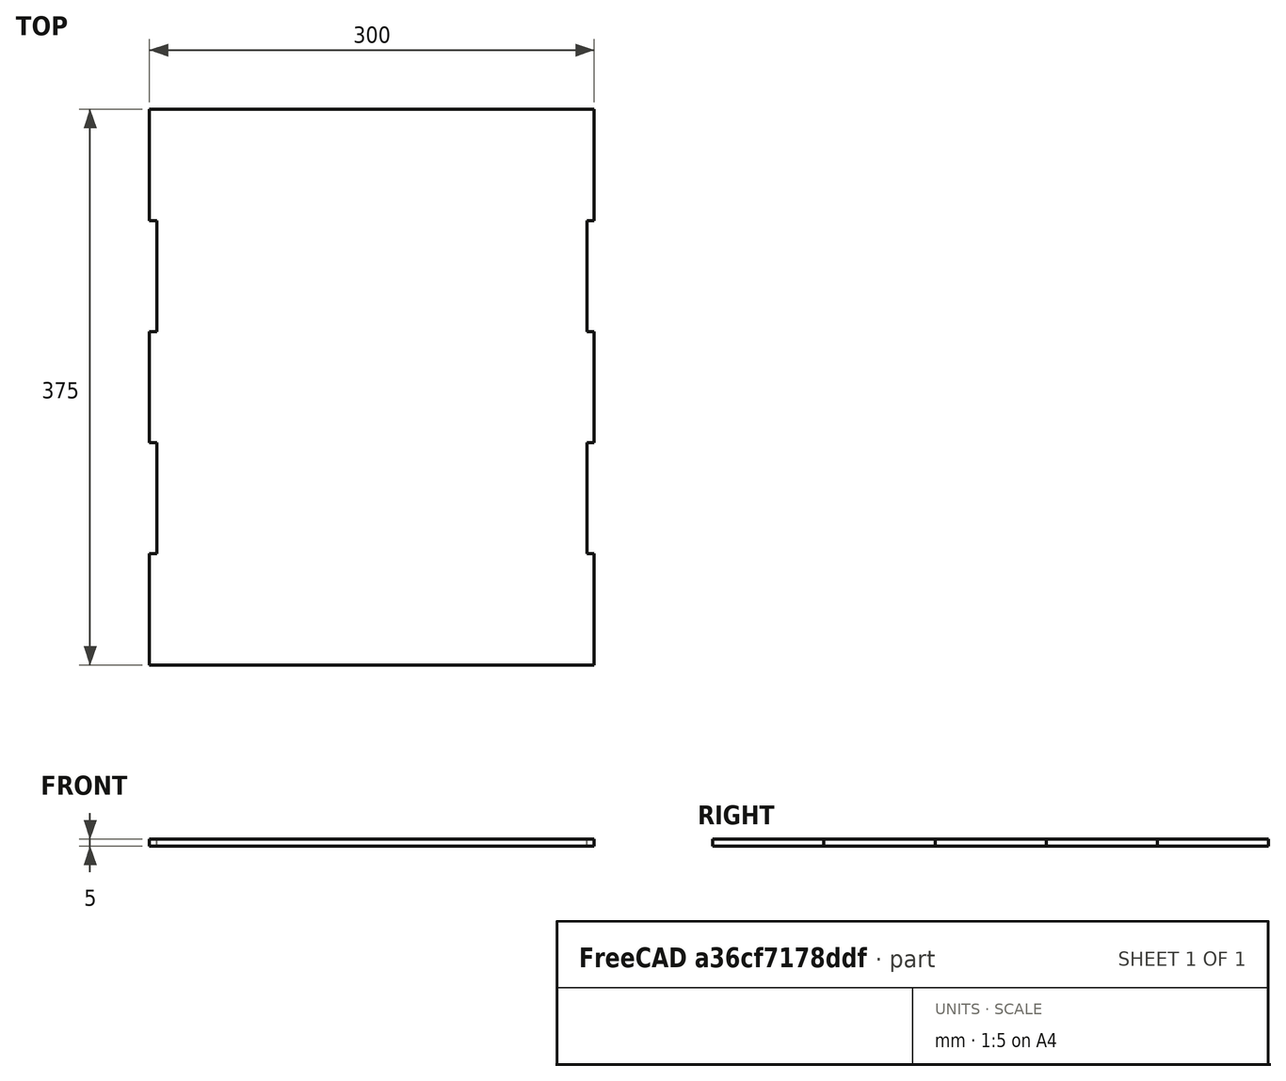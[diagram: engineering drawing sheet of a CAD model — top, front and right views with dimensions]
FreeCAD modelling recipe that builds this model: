
FCSTD DOCUMENT  (FreeCAD 0.18R4 (GitTag))
Label: Chassis
License: All rights reserved
LicenseURL: http://en.wikipedia.org/wiki/All_rights_reserved
objects: Sketcher::SketchObject×2, PartDesign::Pad×1, PartDesign::Body×1
note: 5 computed .brp shape members not serialized (recipe doc carries the construction recipe); baked Part::Feature solids carry a one-line shape summary decoded from their .brp

FEATURE [Sketcher::SketchObject] Sketch
  MapMode = 2
  Support = -> [Sketch]
  sketch-geometry (20):
    g0: LineSegment StartX=-83.8365 StartY=179.356 StartZ=0 EndX=-83.8365 EndY=104.356 EndZ=0
    g1: LineSegment StartX=-83.8365 StartY=104.356 StartZ=0 EndX=-78.8365 EndY=104.356 EndZ=0
    g2: LineSegment StartX=-78.8365 StartY=104.356 StartZ=0 EndX=-78.8365 EndY=29.3556 EndZ=0
    g3: LineSegment StartX=-78.8365 StartY=29.3556 StartZ=0 EndX=-83.8365 EndY=29.3556 EndZ=0
    g4: LineSegment StartX=-83.8365 StartY=29.3556 StartZ=0 EndX=-83.8365 EndY=-45.6444 EndZ=0
    g5: LineSegment StartX=-83.8365 StartY=-45.6444 StartZ=0 EndX=-78.8365 EndY=-45.6444 EndZ=0
    g6: LineSegment StartX=-78.8365 StartY=-45.6444 StartZ=0 EndX=-78.8365 EndY=-120.644 EndZ=0
    g7: LineSegment StartX=-78.8365 StartY=-120.644 StartZ=0 EndX=-83.8365 EndY=-120.644 EndZ=0
    g8: LineSegment StartX=-83.8365 StartY=-120.644 StartZ=0 EndX=-83.8365 EndY=-195.644 EndZ=0
    g9: LineSegment StartX=-83.8365 StartY=-195.644 StartZ=0 EndX=216.163 EndY=-195.644 EndZ=0
    g10: LineSegment StartX=216.163 StartY=-195.644 StartZ=0 EndX=216.163 EndY=-120.644 EndZ=0
    g11: LineSegment StartX=216.163 StartY=-120.644 StartZ=0 EndX=211.163 EndY=-120.644 EndZ=0
    g12: LineSegment StartX=211.163 StartY=-120.644 StartZ=0 EndX=211.163 EndY=-45.6444 EndZ=0
    g13: LineSegment StartX=211.163 StartY=-45.6444 StartZ=0 EndX=216.163 EndY=-45.6444 EndZ=0
    g14: LineSegment StartX=216.163 StartY=-45.6444 StartZ=0 EndX=216.163 EndY=29.3556 EndZ=0
    g15: LineSegment StartX=216.163 StartY=29.3556 StartZ=0 EndX=211.163 EndY=29.3556 EndZ=0
    g16: LineSegment StartX=211.163 StartY=29.3556 StartZ=0 EndX=211.163 EndY=104.356 EndZ=0
    g17: LineSegment StartX=211.163 StartY=104.356 StartZ=0 EndX=216.163 EndY=104.356 EndZ=0
    g18: LineSegment StartX=216.163 StartY=104.356 StartZ=0 EndX=216.163 EndY=179.356 EndZ=0
    g19: LineSegment StartX=216.163 StartY=179.356 StartZ=0 EndX=-83.8365 EndY=179.356 EndZ=0
  constraints (58):
    c: Coincident(g0,g1)
    c: Coincident(g1,g2)
    c: Coincident(g2,g3)
    c: Coincident(g3,g4)
    c: Coincident(g4,g5)
    c: Coincident(g5,g6)
    c: Coincident(g6,g7)
    c: Coincident(g7,g8)
    c: Coincident(g8,g9)
    c: Coincident(g9,g10)
    c: Coincident(g10,g11)
    c: Coincident(g11,g12)
    c: Coincident(g12,g13)
    c: Coincident(g13,g14)
    c: Coincident(g14,g15)
    c: Coincident(g15,g16)
    c: Coincident(g16,g17)
    c: Coincident(g17,g18)
    c: Coincident(g18,g19)
    c: Coincident(g19,g0)
    c: DistanceX(g17,g17) = 5
    c: DistanceX(g15,g15) = 5
    c: DistanceX(g13,g13) = 5
    c: DistanceX(g11,g11) = 5
    c: DistanceX(g7,g7) = 5
    c: DistanceX(g5,g5) = 5
    c: DistanceX(g3,g3) = 5
    c: DistanceX(g1,g1) = 5
    c: Angle(g18,g17) = 1.5708
    c: Angle(g15,g16) = 1.5708
    c: Angle(g19,g16) = 1.5708
    c: Angle(g19,g18) = 1.5708
    c: Angle(g15,g14) = 1.5708
    c: Angle(g12,g13) = 1.5708
    c: Angle(g10,g9) = 1.5708
    c: Angle(g11,g12) = 1.5708
    c: Angle(g12,g9) = 1.5708
    c: Angle(g9,g8) = 1.5708
    c: Angle(g6,g7) = 1.5708
    c: Angle(g5,g6) = 1.5708
    c: Angle(g5,g4) = 1.5708
    c: Angle(g4,g19) = 1.5708
    c: Angle(g0,g19) = 1.5708
    c: Angle(g1,g0) = 1.5708
    c: Angle(g2,g3) = 1.5708
    c: DistanceY(g18,g18) = 75
    c: DistanceY(g0,g0) = 75
    c: DistanceY(g2,g2) = 75
    c: DistanceY(g4,g4) = 75
    c: DistanceY(g6,g6) = 75
    c: DistanceY(g8,g8) = 75
    c: DistanceY(g10,g10) = 75
    c: DistanceY(g12,g12) = 75
    c: DistanceY(g14,g14) = 75
    c: DistanceY(g16,g16) = 75
    c: Angle(g-1,g9) = 0
    c: DistanceX(g19,g19) = 300
    c: DistanceX(g9,g9) = 300
FEATURE [Sketcher::SketchObject] CopySketch
  sketch-geometry (20):
    g0: LineSegment StartX=-83.8365 StartY=179.356 StartZ=0 EndX=-83.8365 EndY=104.356 EndZ=0
    g1: LineSegment StartX=-83.8365 StartY=104.356 StartZ=0 EndX=-78.8365 EndY=104.356 EndZ=0
    g2: LineSegment StartX=-78.8365 StartY=104.356 StartZ=0 EndX=-78.8365 EndY=29.3556 EndZ=0
    g3: LineSegment StartX=-78.8365 StartY=29.3556 StartZ=0 EndX=-83.8365 EndY=29.3556 EndZ=0
    g4: LineSegment StartX=-83.8365 StartY=29.3556 StartZ=0 EndX=-83.8365 EndY=-45.6444 EndZ=0
    g5: LineSegment StartX=-83.8365 StartY=-45.6444 StartZ=0 EndX=-78.8365 EndY=-45.6444 EndZ=0
    g6: LineSegment StartX=-78.8365 StartY=-45.6444 StartZ=0 EndX=-78.8365 EndY=-120.644 EndZ=0
    g7: LineSegment StartX=-78.8365 StartY=-120.644 StartZ=0 EndX=-83.8365 EndY=-120.644 EndZ=0
    g8: LineSegment StartX=-83.8365 StartY=-120.644 StartZ=0 EndX=-83.8365 EndY=-195.644 EndZ=0
    g9: LineSegment StartX=-83.8365 StartY=-195.644 StartZ=0 EndX=216.163 EndY=-195.644 EndZ=0
    g10: LineSegment StartX=216.163 StartY=-195.644 StartZ=0 EndX=216.163 EndY=-120.644 EndZ=0
    g11: LineSegment StartX=216.163 StartY=-120.644 StartZ=0 EndX=211.163 EndY=-120.644 EndZ=0
    g12: LineSegment StartX=211.163 StartY=-120.644 StartZ=0 EndX=211.163 EndY=-45.6444 EndZ=0
    g13: LineSegment StartX=211.163 StartY=-45.6444 StartZ=0 EndX=216.163 EndY=-45.6444 EndZ=0
    g14: LineSegment StartX=216.163 StartY=-45.6444 StartZ=0 EndX=216.163 EndY=29.3556 EndZ=0
    g15: LineSegment StartX=216.163 StartY=29.3556 StartZ=0 EndX=211.163 EndY=29.3556 EndZ=0
    g16: LineSegment StartX=211.163 StartY=29.3556 StartZ=0 EndX=211.163 EndY=104.356 EndZ=0
    g17: LineSegment StartX=211.163 StartY=104.356 StartZ=0 EndX=216.163 EndY=104.356 EndZ=0
    g18: LineSegment StartX=216.163 StartY=104.356 StartZ=0 EndX=216.163 EndY=179.356 EndZ=0
    g19: LineSegment StartX=216.163 StartY=179.356 StartZ=0 EndX=-83.8365 EndY=179.356 EndZ=0
  constraints (58):
    c: Coincident(g0,g1)
    c: Coincident(g1,g2)
    c: Coincident(g2,g3)
    c: Coincident(g3,g4)
    c: Coincident(g4,g5)
    c: Coincident(g5,g6)
    c: Coincident(g6,g7)
    c: Coincident(g7,g8)
    c: Coincident(g8,g9)
    c: Coincident(g9,g10)
    c: Coincident(g10,g11)
    c: Coincident(g11,g12)
    c: Coincident(g12,g13)
    c: Coincident(g13,g14)
    c: Coincident(g14,g15)
    c: Coincident(g15,g16)
    c: Coincident(g16,g17)
    c: Coincident(g17,g18)
    c: Coincident(g18,g19)
    c: Coincident(g19,g0)
    c: DistanceX(g17,g17) = 5
    c: DistanceX(g15,g15) = 5
    c: DistanceX(g13,g13) = 5
    c: DistanceX(g11,g11) = 5
    c: DistanceX(g7,g7) = 5
    c: DistanceX(g5,g5) = 5
    c: DistanceX(g3,g3) = 5
    c: DistanceX(g1,g1) = 5
    c: Angle(g18,g17) = 1.5708
    c: Angle(g15,g16) = 1.5708
    c: Angle(g19,g16) = 1.5708
    c: Angle(g19,g18) = 1.5708
    c: Angle(g15,g14) = 1.5708
    c: Angle(g12,g13) = 1.5708
    c: Angle(g10,g9) = 1.5708
    c: Angle(g11,g12) = 1.5708
    c: Angle(g12,g9) = 1.5708
    c: Angle(g9,g8) = 1.5708
    c: Angle(g6,g7) = 1.5708
    c: Angle(g5,g6) = 1.5708
    c: Angle(g5,g4) = 1.5708
    c: Angle(g4,g19) = 1.5708
    c: Angle(g0,g19) = 1.5708
    c: Angle(g1,g0) = 1.5708
    c: Angle(g2,g3) = 1.5708
    c: DistanceY(g18,g18) = 75
    c: DistanceY(g0,g0) = 75
    c: DistanceY(g2,g2) = 75
    c: DistanceY(g4,g4) = 75
    c: DistanceY(g6,g6) = 75
    c: DistanceY(g8,g8) = 75
    c: DistanceY(g10,g10) = 75
    c: DistanceY(g12,g12) = 75
    c: DistanceY(g14,g14) = 75
    c: DistanceY(g16,g16) = 75
    c: Angle(g-1,g9) = 0
    c: DistanceX(g19,g19) = 300
    c: DistanceX(g9,g9) = 300
FEATURE [PartDesign::Pad] Pad
  Length = 5
  Length2 = 100
  Profile = -> CopySketch
  Type = 0
FEATURE [PartDesign::Body] Body
  Group = -> [Pad]
  Origin = -> Origin
  Tip = -> Pad
